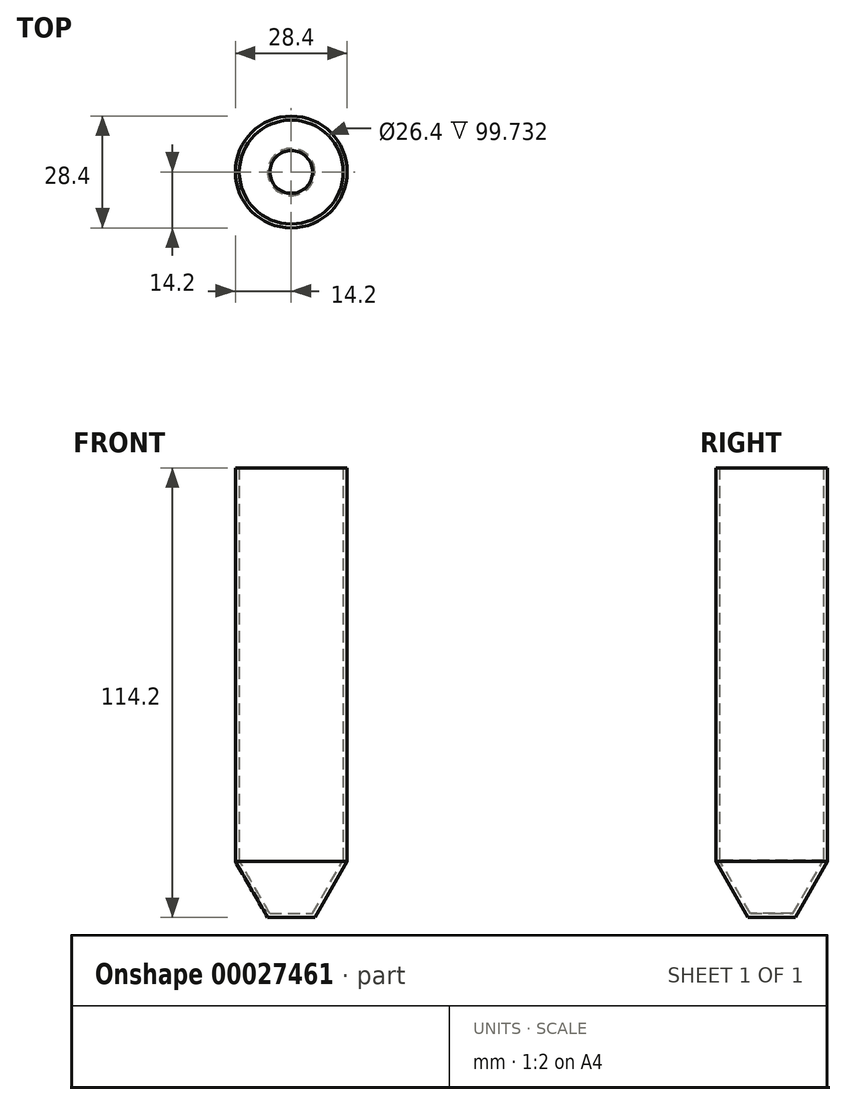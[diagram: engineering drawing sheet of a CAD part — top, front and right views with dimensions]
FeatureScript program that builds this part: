
annotation { "Feature Type Name" : "Feature", "Feature Type Description" : "" }
export const myFeature = defineFeature(function(context is Context, id is Id, definition is map)
    precondition{}
    {
        {
            var Q0;
            Q0=qCreatedBy(makeId("Front.planeOp"),FACE);
            var sketch = newSketch(context, id + "F0", { "sketchPlane" : qUnion([Q0])});
            skLineSegment(sketch, "E0", {"start": v(14.2, 57.55) * mm, "end": v(14.2, -42.45) * mm});
            skLineSegment(sketch, "E1", {"start": v(14.2, -42.45) * mm, "end": v(6, -56.65) * mm});
            skLineSegment(sketch, "E2", {"start": v(6, -56.65) * mm, "end": v(0, -56.65) * mm});
            skLineSegment(sketch, "E3.0", {"start": v(5.42, -55.65) * mm, "end": v(0, -55.65) * mm});
            skLineSegment(sketch, "E3.1", {"start": v(13.2, -42.18) * mm, "end": v(5.42, -55.65) * mm});
            skLineSegment(sketch, "E3.2", {"start": v(13.2, 57.55) * mm, "end": v(13.2, -42.18) * mm});
            skLineSegment(sketch, "E4", {"start": v(13.2, 57.55) * mm, "end": v(14.2, 57.55) * mm});
            skLineSegment(sketch, "E5", {"start": v(0, -56.65) * mm, "end": v(0, -55.65) * mm});
            skLineSegment(sketch, "E6", {"start": v(0, -56.65) * mm, "end": v(0, 57.55) * mm, "construction": true});
            skSolve(sketch);
        }
        {
            var Q0;
            Q0=qSketchRegion(id+"F0",true);
            var Q1;
            Q1=sQuery(id+"F0.wireOp",EDGE,"E6");
            revolve(context, id + "F1", {"entities" : qUnion([Q0]), "axis" : qUnion([Q1]), "revolveType" : RevolveType.FULL});
        }
    });
